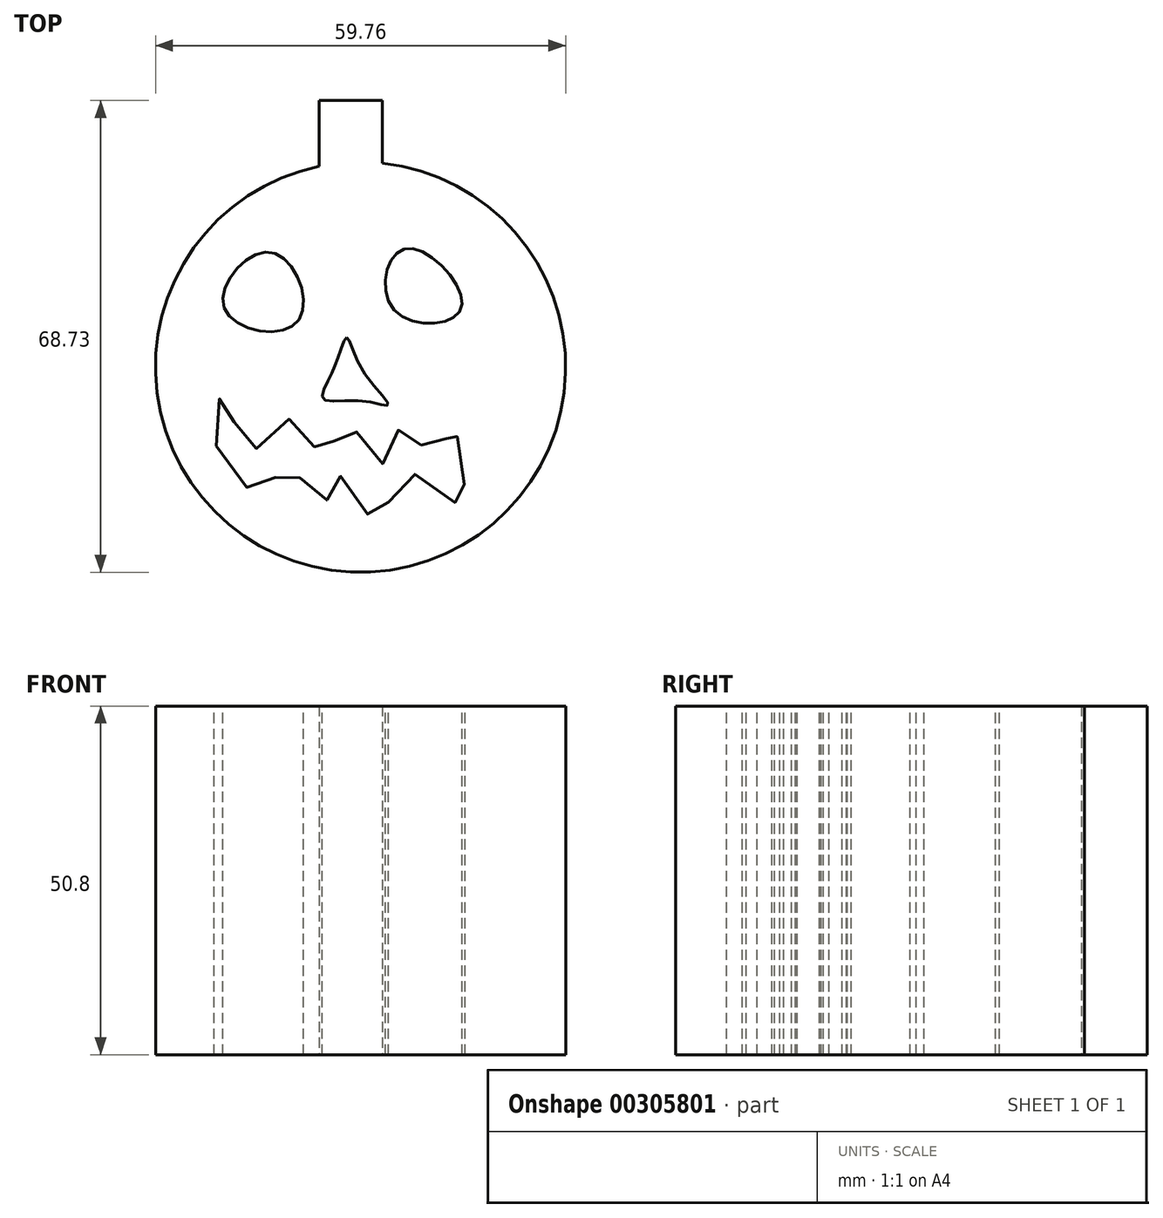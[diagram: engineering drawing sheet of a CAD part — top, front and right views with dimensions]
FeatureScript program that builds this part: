
annotation { "Feature Type Name" : "Feature", "Feature Type Description" : "" }
export const myFeature = defineFeature(function(context is Context, id is Id, definition is map)
    precondition{}
    {
        {
            var Q0;
            Q0=qCreatedBy(makeId("Top.planeOp"),FACE);
            var sketch = newSketch(context, id + "F0", { "sketchPlane" : qUnion([Q0])});
            skCircle(sketch, "E0", {"center": v(-37.7, 22.45) * mm, "radius": 29.88 * mm});
            skSolve(sketch);
        }
        {
            var Q0;
            Q0 = qSketchRegion(id + "F0", true);
            extrude(context, id + "F1", {"entities" : qUnion([Q0]), "depth" : 50.8 * mm});
        }
        {
            var Q0;
            Q0=makeQuery(id+"F1.opExtrude","CAP_FACE",FACE,{"disambiguationData":[OSD([sQuery(id+"F0.wireOp",EDGE,"E0")])],"isStart":false});
            var sketch = newSketch(context, id + "F2", { "sketchPlane" : qUnion([Q0])});
            skFitSpline(sketch, "E1", {"points": [v(-32.8, 30.8) * mm, v(-31.08, 39.72) * mm, v(-23.02, 31.08) * mm, v(-32.8, 30.8) * mm]});
            skSolve(sketch);
        }
        {
            var Q0;
            Q0 = qSketchRegion(id + "F2", true);
            extrude(context, id + "F3", {"entities" : qUnion([Q0]), "operationType" : NewBodyOperationType.REMOVE, "oppositeDirection" : true, "depth" : 50.8 * mm});
        }
        {
            var Q0;
            Q0=makeQuery(id+"F1.opExtrude","CAP_FACE",FACE,{"disambiguationData":[OSD([sQuery(id+"F0.wireOp",EDGE,"E0")])],"isStart":false});
            var sketch = newSketch(context, id + "F4", { "sketchPlane" : qUnion([Q0])});
            skFitSpline(sketch, "E2", {"points": [v(-57.56, 31.08) * mm, v(-50.65, 39.14) * mm, v(-46.91, 29.07) * mm, v(-57.56, 31.08) * mm]});
            skSolve(sketch);
        }
        {
            var Q0;
            Q0 = qSketchRegion(id + "F4", true);
            extrude(context, id + "F5", {"entities" : qUnion([Q0]), "operationType" : NewBodyOperationType.REMOVE, "oppositeDirection" : true, "depth" : 50.8 * mm});
        }
        {
            var Q0;
            Q0=makeQuery(id+"F1.opExtrude","CAP_FACE",FACE,{"disambiguationData":[OSD([sQuery(id+"F0.wireOp",EDGE,"E0")])],"isStart":false});
            var sketch = newSketch(context, id + "F6", { "sketchPlane" : qUnion([Q0])});
            skFitSpline(sketch, "E3", {"points": [v(-39.72, 26.77) * mm, v(-40.87, 24.18) * mm, v(-42.3, 20.72) * mm, v(-43.17, 17.84) * mm, v(-37.7, 17.56) * mm, v(-33.67, 16.98) * mm, v(-37.7, 22.45) * mm, v(-39.72, 26.77) * mm]});
            skSolve(sketch);
        }
        {
            var Q0;
            Q0 = qSketchRegion(id + "F6", true);
            extrude(context, id + "F7", {"entities" : qUnion([Q0]), "operationType" : NewBodyOperationType.REMOVE, "oppositeDirection" : true, "depth" : 50.8 * mm});
        }
        {
            var Q0;
            Q0=makeQuery(id+"F1.opExtrude","CAP_FACE",FACE,{"disambiguationData":[OSD([sQuery(id+"F0.wireOp",EDGE,"E0")])],"isStart":false});
            var sketch = newSketch(context, id + "F8", { "sketchPlane" : qUnion([Q0])});
            skFitSpline(sketch, "E4", {"points": [v(-58.71, 10.94) * mm, v(-51.8, 4.6) * mm, v(-48.35, 7.77) * mm, v(-42.88, 2.88) * mm, v(-40.87, 6.62) * mm, v(-35.4, 0) * mm, v(-31.08, 6.9) * mm, v(-23.02, 2.3) * mm, v(-23.31, 9.79) * mm, v(-24.18, 13.53) * mm, v(-27.34, 10.07) * mm, v(-31.66, 13.81) * mm, v(-34.54, 8.35) * mm, v(-39.72, 14.1) * mm, v(-43.17, 9.5) * mm, v(-47.49, 14.97) * mm, v(-53.82, 10.36) * mm, v(-57.56, 18.13) * mm, v(-58.71, 10.94) * mm]});
            skSolve(sketch);
        }
        {
            var Q0;
            Q0 = qSketchRegion(id + "F8", true);
            extrude(context, id + "F9", {"entities" : qUnion([Q0]), "operationType" : NewBodyOperationType.REMOVE, "oppositeDirection" : true, "depth" : 50.8 * mm});
        }
        {
            var Q0;
            Q0=qCreatedBy(makeId("Top.planeOp"),FACE);
            var sketch = newSketch(context, id + "F10", { "sketchPlane" : qUnion([Q0])});
            skLineSegment(sketch, "E5.bottom", {"start": v(-43.75, 61.3) * mm, "end": v(-34.54, 61.3) * mm});
            skLineSegment(sketch, "E5.top", {"start": v(-43.75, 51.23) * mm, "end": v(-34.54, 51.23) * mm});
            skLineSegment(sketch, "E5.left", {"start": v(-43.75, 61.3) * mm, "end": v(-43.75, 51.23) * mm});
            skLineSegment(sketch, "E5.right", {"start": v(-34.54, 61.3) * mm, "end": v(-34.54, 51.23) * mm});
            skSolve(sketch);
        }
        {
            var Q0;
            Q0 = qSketchRegion(id + "F10", true);
            extrude(context, id + "F11", {"entities" : qUnion([Q0]), "operationType" : NewBodyOperationType.ADD, "depth" : 50.8 * mm});
        }
    });
